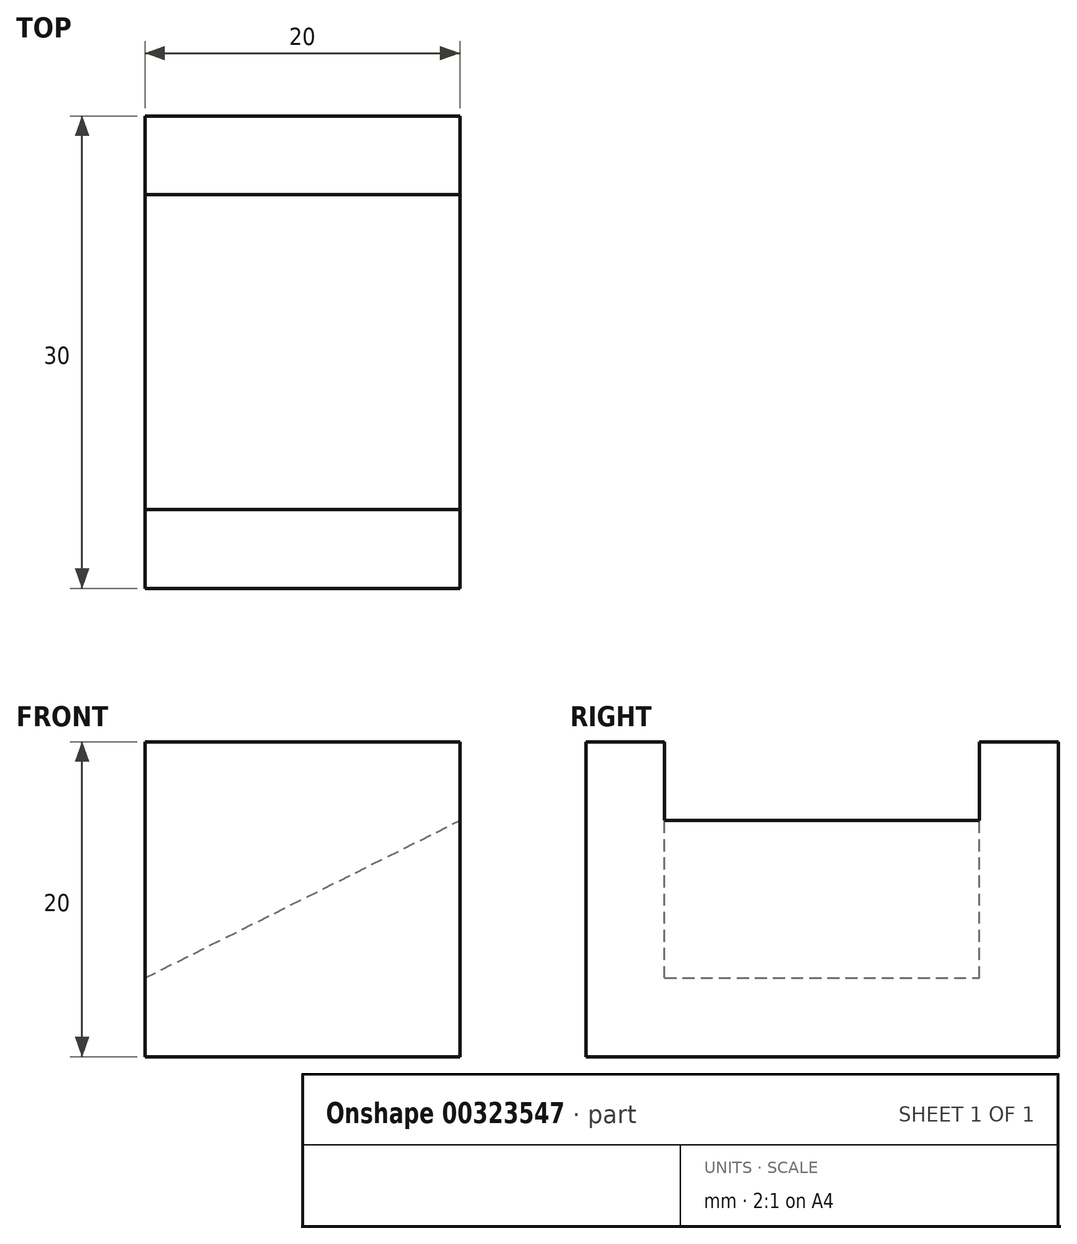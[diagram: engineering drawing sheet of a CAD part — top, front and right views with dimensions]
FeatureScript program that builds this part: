
annotation { "Feature Type Name" : "Feature", "Feature Type Description" : "" }
export const myFeature = defineFeature(function(context is Context, id is Id, definition is map)
    precondition{}
    {
        {
            var Q0;
            Q0=qCreatedBy(makeId("Front.planeOp"),FACE);
            var sketch = newSketch(context, id + "F0", { "sketchPlane" : qUnion([Q0])});
            skLineSegment(sketch, "E0", {"start": v(0, 0) * mm, "end": v(0, 20) * mm});
            skLineSegment(sketch, "E1", {"start": v(0, 20) * mm, "end": v(20, 20) * mm});
            skLineSegment(sketch, "E2", {"start": v(20, 20) * mm, "end": v(20, 0) * mm});
            skLineSegment(sketch, "E3", {"start": v(20, 0) * mm, "end": v(0, 0) * mm});
            skSolve(sketch);
        }
        {
            var Q0;
            Q0 = qSketchRegion(id + "F0", true);
            extrude(context, id + "F1", {"entities" : qUnion([Q0]), "depth" : 5 * mm});
        }
        {
            var Q0;
            Q0=makeQuery(id+"F1.opExtrude","CAP_FACE",FACE,{"disambiguationData":[OSD([sQuery(id+"F0.wireOp",EDGE,"E0"),sQuery(id+"F0.wireOp",EDGE,"E1"),sQuery(id+"F0.wireOp",EDGE,"E2"),sQuery(id+"F0.wireOp",EDGE,"E3")])],"isStart":false});
            var sketch = newSketch(context, id + "F2", { "sketchPlane" : qUnion([Q0])});
            skLineSegment(sketch, "E4", {"start": v(0, 0) * mm, "end": v(0, 5) * mm});
            skLineSegment(sketch, "E5", {"start": v(0, 5) * mm, "end": v(20, 15) * mm});
            skLineSegment(sketch, "E6", {"start": v(20, 15) * mm, "end": v(20, 0) * mm});
            skLineSegment(sketch, "E7", {"start": v(20, 0) * mm, "end": v(0, 0) * mm});
            skSolve(sketch);
        }
        {
            var Q0;
            Q0 = qSketchRegion(id + "F2", true);
            extrude(context, id + "F3", {"entities" : qUnion([Q0]), "operationType" : NewBodyOperationType.ADD, "depth" : 20 * mm});
        }
        {
            var Q0;
            Q0=makeQuery(id+"F3.opExtrude","CAP_FACE",FACE,{"disambiguationData":[OSD([sQuery(id+"F2.wireOp",EDGE,"E4"),sQuery(id+"F2.wireOp",EDGE,"E5"),sQuery(id+"F2.wireOp",EDGE,"E6"),sQuery(id+"F2.wireOp",EDGE,"E7")])],"isStart":false});
            var sketch = newSketch(context, id + "F4", { "sketchPlane" : qUnion([Q0])});
            skLineSegment(sketch, "E8", {"start": v(0, 0) * mm, "end": v(0, 20) * mm});
            skPoint(sketch, "E8.endSnap0", {"position": v(0, 2.5) * mm});
            skLineSegment(sketch, "E9", {"start": v(0, 20) * mm, "end": v(20, 20) * mm});
            skLineSegment(sketch, "E10", {"start": v(20, 20) * mm, "end": v(20, 0) * mm});
            skLineSegment(sketch, "E11", {"start": v(20, 0) * mm, "end": v(0, 0) * mm});
            skSolve(sketch);
        }
        {
            var Q0;
            Q0 = qSketchRegion(id + "F4", true);
            extrude(context, id + "F5", {"entities" : qUnion([Q0]), "operationType" : NewBodyOperationType.ADD, "depth" : 5 * mm});
        }
    });
